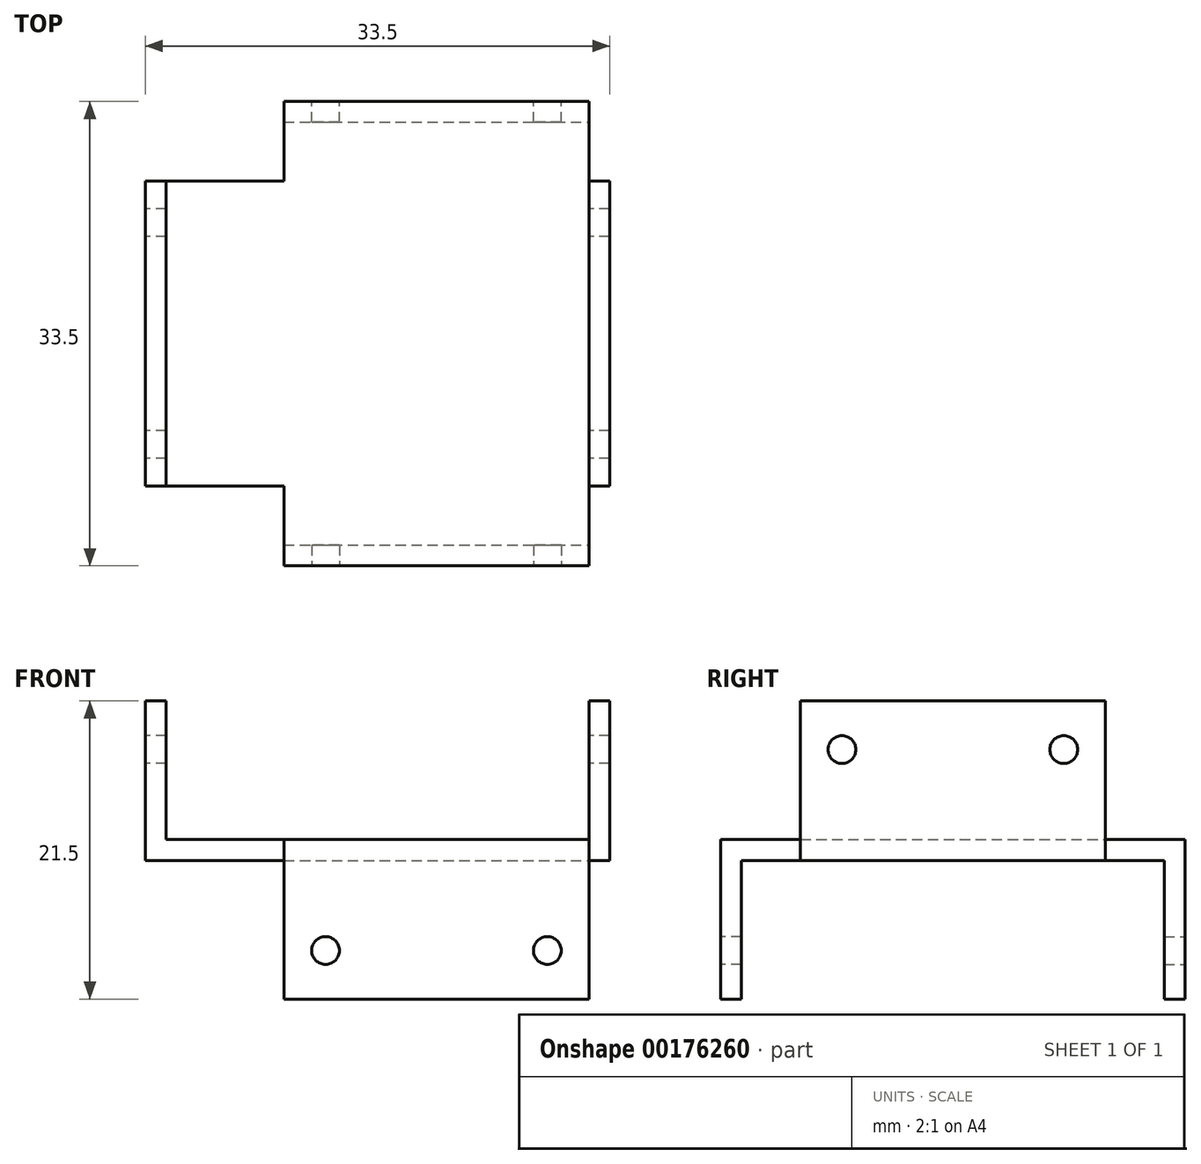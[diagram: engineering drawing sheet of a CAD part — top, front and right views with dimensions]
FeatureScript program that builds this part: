
annotation { "Feature Type Name" : "Feature", "Feature Type Description" : "" }
export const myFeature = defineFeature(function(context is Context, id is Id, definition is map)
    precondition{}
    {
        {
            var Q0;
            Q0=qCreatedBy(makeId("Top.planeOp"),FACE);
            var sketch = newSketch(context, id + "F0", { "sketchPlane" : qUnion([Q0])});
            skLineSegment(sketch, "E0.bottom", {"start": v(-16.75, 11) * mm, "end": v(16.75, 11) * mm});
            skLineSegment(sketch, "E0.top", {"start": v(-16.75, -11) * mm, "end": v(16.75, -11) * mm});
            skLineSegment(sketch, "E0.left", {"start": v(-16.75, 11) * mm, "end": v(-16.75, -11) * mm});
            skLineSegment(sketch, "E0.right", {"start": v(16.75, 11) * mm, "end": v(16.75, -11) * mm});
            skPoint(sketch, "E0.middle", {"position": v(0, 0) * mm});
            skLineSegment(sketch, "E1.bottom", {"start": v(-6.75, 16.75) * mm, "end": v(15.25, 16.75) * mm});
            skLineSegment(sketch, "E1.top", {"start": v(-6.75, -16.75) * mm, "end": v(15.25, -16.75) * mm});
            skLineSegment(sketch, "E1.left", {"start": v(-6.75, 16.75) * mm, "end": v(-6.75, -16.75) * mm});
            skLineSegment(sketch, "E1.right", {"start": v(15.25, 16.75) * mm, "end": v(15.25, -16.75) * mm});
            skPoint(sketch, "E1.middle", {"position": v(4.25, 0) * mm});
            skSolve(sketch);
        }
        {
            var Q0;
            Q0 = qSketchRegion(id + "F0", true);
            extrude(context, id + "F1", {"entities" : qUnion([Q0]), "depth" : (1.5 / 2) * mm, "hasSecondDirection" : true, "secondDirectionOppositeDirection" : true, "secondDirectionDepth" : (1.5 / 2) * mm});
        }
        {
            var Q0;
            Q0=makeQuery(id+"F1.opExtrude","CAP_FACE",FACE,{"disambiguationData":[OSD([sQuery(id+"F0.wireOp",EDGE,"E0.bottom"),sQuery(id+"F0.wireOp",EDGE,"E0.top"),sQuery(id+"F0.wireOp",EDGE,"E0.left"),sQuery(id+"F0.wireOp",EDGE,"E0.right")])],"isStart":false});
            var sketch = newSketch(context, id + "F2", { "sketchPlane" : qUnion([Q0])});
            skLineSegment(sketch, "E2.bottom", {"start": v(-16.75, -11) * mm, "end": v(-15.25, -11) * mm});
            skLineSegment(sketch, "E2.top", {"start": v(-16.75, 11) * mm, "end": v(-15.25, 11) * mm});
            skLineSegment(sketch, "E2.left", {"start": v(-16.75, -11) * mm, "end": v(-16.75, 11) * mm});
            skLineSegment(sketch, "E2.right", {"start": v(-15.25, -11) * mm, "end": v(-15.25, 11) * mm});
            skLineSegment(sketch, "E3.MirrorCS", {"start": v(16.75, -11) * mm, "end": v(15.25, -11) * mm});
            skLineSegment(sketch, "E4.MirrorCS", {"start": v(16.75, 11) * mm, "end": v(15.25, 11) * mm});
            skLineSegment(sketch, "E5.MirrorCS", {"start": v(16.75, -11) * mm, "end": v(16.75, 11) * mm});
            skLineSegment(sketch, "E6.MirrorCS", {"start": v(15.25, -11) * mm, "end": v(15.25, 11) * mm});
            skSolve(sketch);
        }
        {
            var Q0;
            Q0 = qSketchRegion(id + "F2", true);
            extrude(context, id + "F3", {"entities" : qUnion([Q0]), "operationType" : NewBodyOperationType.ADD, "depth" : 10 * mm});
        }
        {
            var Q0;
            Q0=makeQuery(id+"F1.opExtrude","CAP_FACE",FACE,{"disambiguationData":[OSD([sQuery(id+"F0.wireOp",EDGE,"E0.bottom"),sQuery(id+"F0.wireOp",EDGE,"E0.top"),sQuery(id+"F0.wireOp",EDGE,"E0.left"),sQuery(id+"F0.wireOp",EDGE,"E0.right"),sQuery(id+"F0.wireOp",EDGE,"E1.bottom"),sQuery(id+"F0.wireOp",EDGE,"E1.top"),sQuery(id+"F0.wireOp",EDGE,"E1.left"),sQuery(id+"F0.wireOp",EDGE,"E1.right")])],"isStart":true});
            var sketch = newSketch(context, id + "F4", { "sketchPlane" : qUnion([Q0])});
            skLineSegment(sketch, "E7.bottom", {"start": v(-6.75, 16.75) * mm, "end": v(15.25, 16.75) * mm});
            skLineSegment(sketch, "E7.top", {"start": v(-6.75, 15.25) * mm, "end": v(15.25, 15.25) * mm});
            skLineSegment(sketch, "E7.left", {"start": v(-6.75, 16.75) * mm, "end": v(-6.75, 15.25) * mm});
            skLineSegment(sketch, "E7.right", {"start": v(15.25, 16.75) * mm, "end": v(15.25, 15.25) * mm});
            skSolve(sketch);
        }
        {
            var Q0;
            Q0 = qSketchRegion(id + "F4", true);
            extrude(context, id + "F5", {"entities" : qUnion([Q0]), "operationType" : NewBodyOperationType.ADD, "depth" : 10 * mm});
        }
        {
            var Q0;
            Q0=makeQuery(id+"F3.opExtrude","SWEPT_FACE",FACE,{"disambiguationData":[OSD([sQuery(id+"F2.wireOp",EDGE,"E2.right")])]});
            var sketch = newSketch(context, id + "F6", { "sketchPlane" : qUnion([Q0])});
            skLineSegment(sketch, "E8", {"start": v(-11, 7.25) * mm, "end": v(11, 7.25) * mm, "construction": true});
            skCircle(sketch, "E9", {"center": v(-8, 7.25) * mm, "radius": 1 * mm});
            skCircle(sketch, "E10.MirrorC", {"center": v(8, 7.25) * mm, "radius": 1 * mm});
            skSolve(sketch);
        }
        {
            var Q0;
            Q0 = qSketchRegion(id + "F6", true);
            extrude(context, id + "F7", {"entities" : qUnion([Q0]), "operationType" : NewBodyOperationType.REMOVE, "endBound" : BoundingType.THROUGH_ALL, "depth" : 25 * mm, "hasSecondDirection" : true, "secondDirectionBound" : SecondDirectionBoundingType.UP_TO_NEXT, "secondDirectionOppositeDirection" : true, "secondDirectionDepth" : 25 * mm});
        }
        {
            var Q0;
            Q0=makeQuery(id+"F5.boolean.opBoolean","MERGE",FACE,{"derivedFrom":[makeQuery(id+"F1.opExtrude","SWEPT_FACE",FACE,{"disambiguationData":[OSD([sQuery(id+"F0.wireOp",EDGE,"E1.top")])]}),makeQuery(id+"F5.opExtrude","SWEPT_FACE",FACE,{"disambiguationData":[OSD([sQuery(id+"F4.wireOp",EDGE,"E7.bottom")])]})]});
            var sketch = newSketch(context, id + "F8", { "sketchPlane" : qUnion([Q0])});
            skLineSegment(sketch, "E11", {"start": v(-6.75, -7.25) * mm, "end": v(15.25, -7.25) * mm, "construction": true});
            skCircle(sketch, "E12", {"center": v(-3.75, -7.25) * mm, "radius": 1 * mm});
            skLineSegment(sketch, "E13", {"start": v(4.25, -10.75) * mm, "end": v(4.25, 0.75) * mm, "construction": true});
            skCircle(sketch, "E14.MirrorC", {"center": v(12.25, -7.25) * mm, "radius": 1 * mm});
            skSolve(sketch);
        }
        {
            var Q0;
            Q0 = qSketchRegion(id + "F8", true);
            extrude(context, id + "F9", {"entities" : qUnion([Q0]), "operationType" : NewBodyOperationType.REMOVE, "endBound" : BoundingType.UP_TO_NEXT, "oppositeDirection" : true, "depth" : 25 * mm});
        }
        {
            var Q0;
            Q0=makeQuery(id+"F1.opExtrude","SWEPT_BODY",BODY,{"disambiguationData":[OSD([sQuery(id+"F0.wireOp",EDGE,"E0.bottom"),sQuery(id+"F0.wireOp",EDGE,"E0.top"),sQuery(id+"F0.wireOp",EDGE,"E0.left"),sQuery(id+"F0.wireOp",EDGE,"E0.right"),sQuery(id+"F0.wireOp",EDGE,"E1.bottom"),sQuery(id+"F0.wireOp",EDGE,"E1.top"),sQuery(id+"F0.wireOp",EDGE,"E1.left"),sQuery(id+"F0.wireOp",EDGE,"E1.right")])]});
            var Q1;
            Q1=qCreatedBy(makeId("Front.planeOp"),FACE);
            mirror(context, id + "F10", {"operationType" : NewBodyOperationType.ADD, "entities" : qUnion([Q0]), "mirrorPlane" : qUnion([Q1])});
        }
    });
